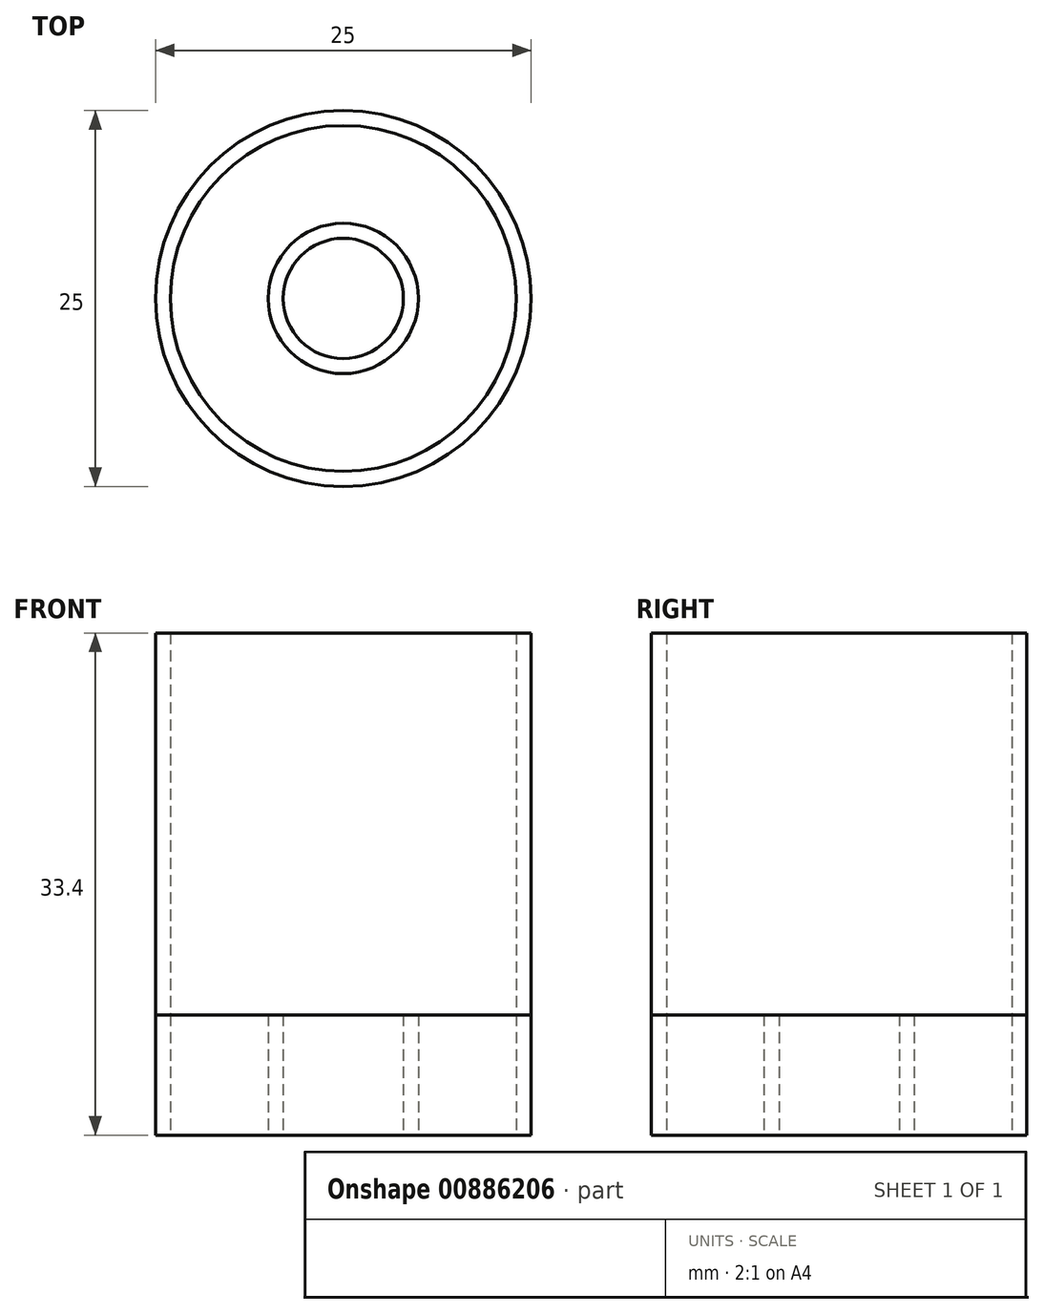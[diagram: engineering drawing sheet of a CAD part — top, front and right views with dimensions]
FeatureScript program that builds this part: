
annotation { "Feature Type Name" : "Feature", "Feature Type Description" : "" }
export const myFeature = defineFeature(function(context is Context, id is Id, definition is map)
    precondition{}
    {
        {
            var Q0;
            Q0=qCreatedBy(makeId("Top.planeOp"),FACE);
            var sketch = newSketch(context, id + "F0", { "sketchPlane" : qUnion([Q0])});
            skCircle(sketch, "E0", {"center": v(0, 0) * mm, "radius": 12.5 * mm});
            skCircle(sketch, "E1", {"center": v(0, 0) * mm, "radius": 11.5 * mm});
            skCircle(sketch, "E2", {"center": v(0, 0) * mm, "radius": 5 * mm});
            skCircle(sketch, "E3", {"center": v(0, 0) * mm, "radius": 4 * mm});
            skSolve(sketch);
        }
        {
            var Q0;
            Q0=makeQuery(id+"F0.imprint","IMPRINT",FACE,{"disambiguationData":[TD([[makeQuery(id+"F0.imprint","IMPRINT",EDGE,{"derivedFrom":sQuery(id+"F0.wireOp",EDGE,"E0")}),1.0]])]});
            var Q1;
            Q1=makeQuery(id+"F0.imprint","IMPRINT",FACE,{"disambiguationData":[TD([[makeQuery(id+"F0.imprint","IMPRINT",EDGE,{"derivedFrom":sQuery(id+"F0.wireOp",EDGE,"E2")}),1.0]])]});
            extrude(context, id + "F1", {"entities" : qUnion([Q0, Q1]), "endBound" : BoundingType.SYMMETRIC, "depth" : 8 * mm, "offsetDistance" : 25.4 * mm});
        }
        {
            var Q0;
            Q0=makeQuery(id+"F1.opExtrude","CAP_FACE",FACE,{"disambiguationData":[OSD([sQuery(id+"F0.wireOp",EDGE,"E2"),sQuery(id+"F0.wireOp",EDGE,"E3")])],"isStart":false});
            var sketch = newSketch(context, id + "F2", { "sketchPlane" : qUnion([Q0])});
            skSolve(sketch);
        }
        {
            var Q0;
            Q0=makeQuery(id+"F2.imprint","IMPRINT",FACE,{"disambiguationData":[TD([[makeQuery(id+"F2.imprint","IMPRINT",EDGE,{"derivedFrom":makeQuery(id+"F1.opExtrude","CAP_EDGE",EDGE,{"disambiguationData":[OSD([sQuery(id+"F0.wireOp",EDGE,"E2")])],"isStart":false})}),1.0]])]});
            var Q1;
            Q1=makeQuery(id+"F1.opExtrude","CAP_FACE",FACE,{"disambiguationData":[OSD([sQuery(id+"F0.wireOp",EDGE,"E0"),sQuery(id+"F0.wireOp",EDGE,"E1")])],"isStart":false});
            extrude(context, id + "F3", {"entities" : qUnion([Q0, Q1]), "depth" : 25.4 * mm, "offsetDistance" : 25.4 * mm});
        }
    });
